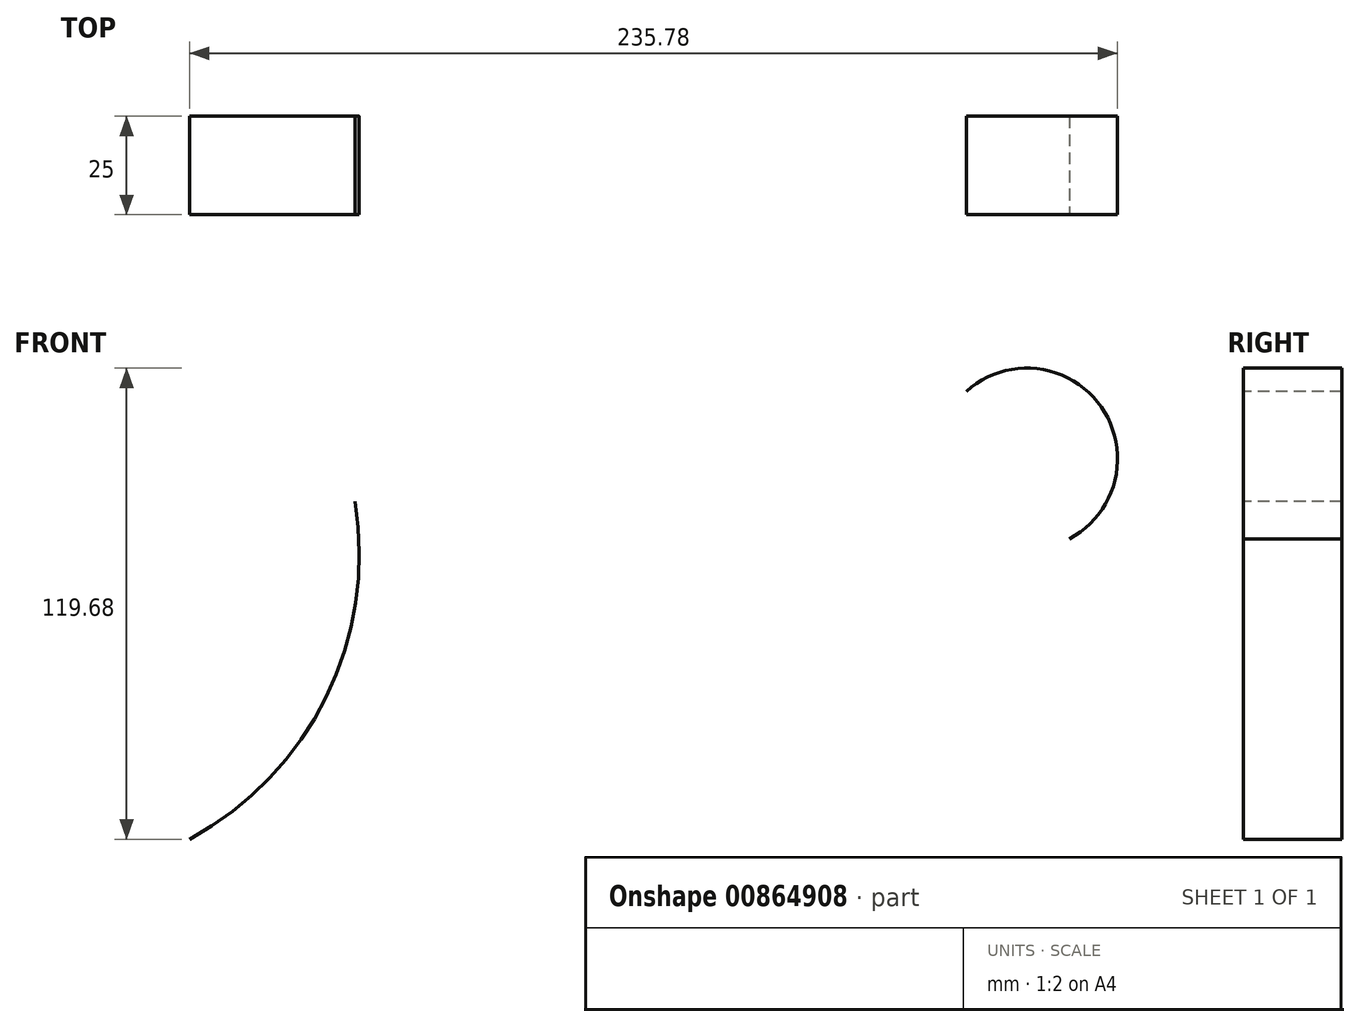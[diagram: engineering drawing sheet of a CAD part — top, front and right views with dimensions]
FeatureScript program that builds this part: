
annotation { "Feature Type Name" : "Feature", "Feature Type Description" : "" }
export const myFeature = defineFeature(function(context is Context, id is Id, definition is map)
    precondition{}
    {
        {
            var Q0;
            Q0=qCreatedBy(makeId("Front.planeOp"),FACE);
            var sketch = newSketch(context, id + "F0", { "sketchPlane" : qUnion([Q0])});
            skArc(sketch, "E0", {"start": v(-159.85, -43.62) * mm, "mid": v(-125.1, -7.48) * mm, "end": v(-117.83, 42.13) * mm});
            skArc(sketch, "E1", {"start": v(63.7, 32.68) * mm, "mid": v(71.76, 66.23) * mm, "end": v(37.48, 70.16) * mm});
            skSolve(sketch);
        }
        {
            var Q0;
            Q0=sQuery(id+"F0.wireOp",EDGE,"E0");
            var Q1;
            Q1=sQuery(id+"F0.wireOp",EDGE,"E1");
            extrude(context, id + "F1", {"bodyType" : ToolBodyType.SURFACE, "surfaceEntities" : qUnion([Q0, Q1]), "depth" : 25 * mm, "offsetDistance" : 25 * mm});
        }
    });
